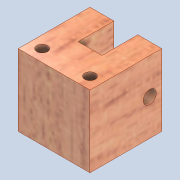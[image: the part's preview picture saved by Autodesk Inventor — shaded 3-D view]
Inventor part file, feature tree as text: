
AUTODESK INVENTOR PART (.ipt)
format: ipt  version: 2020 (Build 240168000, 168)  size: 187,904 bytes
history: native  units: mm
features: sketch x4, extrude x3, hole x1, projected_geometry x1
ambient origin geometry x8: Origin, YZ Plane, XZ Plane, XY Plane, X Axis, Y Axis, Z Axis, Center Point
bodies: Solid1 (feature_tree)
feature tree (9):
  extrude  "Extrusion1"  Depth=30.0mm
  extrude  "Extrusion3"  Depth=10.0mm
  hole  "Hole1"  [1 undecoded]
  extrude  "Extrusion6"  Depth=4.5mm
  sketch  "Sketch1"  dims[d0=30.0mm d1=30.0mm]
  sketch  "Sketch4"  dims[d2=30.0mm d3=0.0mm d8=10.0mm]
  sketch  "Sketch5"  dims[d9=15.0mm d10=0.0mm d11=5.0mm]
  sketch  "Sketch8"  dims[d12=5.5mm d13=6.0mm d14=4.0mm d15=2.0mm d16=90.0deg d17=8.0mm d18=20.594885mm d28=4.5mm d30=5.0mm d31=5.0mm d32=5.0mm d33=0.0mm d34=0.0mm]
  projected_geometry  "Projected Loop1"
note: 1 required parameter value undecoded (feature->parameter linkage not recoverable at this tier; creation-order binding heuristic only, values carry confidence <= 0.55)
